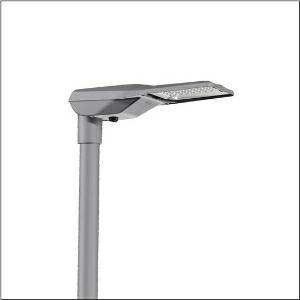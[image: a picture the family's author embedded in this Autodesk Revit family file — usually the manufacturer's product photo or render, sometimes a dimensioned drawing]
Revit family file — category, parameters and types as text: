
# Revit family: streetlight_sl_21_mini___p0_8a_5xe2u33r08gb_ec99
name_source: partatom
category: Lighting Fixtures
units: mm (PartAtom-declared; Revit-internal decimal feet)

## family parameters
Cut with Voids When Loaded = No
Host = Face
Light Source = No
Part Type = Normal
Room Calculation Point = No
Round Connector Dimension = Use Diameter
Shared = No

## types (1)
- --- (1 x LED, 5990 lm, 40.4 W, 3000K)
    Apparent Load = 40 VA
    CIE Flux Codes = 33 69 96 100 100
    Color Rendering = 70
    Color Temperature = 3000K
    Default Elevation = 1800 mm
    Description = Streetlight SL 21 mini, mast luminaire, primary light control with lens, of PMMA, primary optical cover: cover, of toughened safety glass, transparent, light distribution: P0.8a, light emission: direct distribution, primary light characteristic: asymmetric, installation type: post-top, side-entry, LED, High Power LED, rated luminous flux: 5.990lm, luminous efficacy: 148lm/W, light colour: 730, colour temperature: 3000K, control gear: D4i, control: pre-setting: logarithmic dimming characteristic, flexible luminous flux parameterisation, time-dependent luminous flux control, constant luminous flux control, overheat protection, mains connection: 220..240V, AC, 50/60Hz, start of lifetime: 40W, end of service life: 41W, reduction: 19W, luminaire housing, of diecast aluminium, powder-coated, Siteco® metallic grey (DB 702S), corrosivity category C5 mid according to DIN EN ISO 12944, multi-level sealing system, sealing non-destructively replaceable, inclination adjustable: 0°, 5°, 10°, 15°, please order mast flange separately, length: 628mm, width: 235mm, height: 110mm, mast flange for spigot size: 42mm (side-entry): 5XC10008XM4, 60/48mm (side-entry/post-top): 5XC10108XM2, 76/60mm (side-entry/post-top): 5XC10108XM1, mounting height: 4..8m, Smart Interface below, protection rating (complete): IP66, insulation class (complete): insulation class II (safety insulation), certification: CE, ENEC, ENEC+, VDE, impact resistance: IK10, permissible operating ambient temperature for outdoor applications: -40..+50°C, standard-compliant lighting for roads and squares, packaging unit: 1 piece

Light Distribution: P0.8a
    Height = 110 mm
    Lamp = 1 x LED
    Lamp Light Flux = 5990 lm
    Lamp Power = 40.4 W
    Lamp count = 1
    Length = 625 mm
    Luminous efficacy = 148 lm/W
    Manufacturer = Siteco
    ModVariant = No
    Model = 5XE2U33R08GB
    Number of Poles = 1
    OnlyDefault = Yes
    Power Factor = 1
    Product Name = Streetlight SL 21 mini | P0.8a
    Product group = mast luminaire | pylon top
    ProductGroupID = 6100
    Protection Class = Protection class II
    Protection Degree = IP 66
    RLX_Detail_Level = 1
    RLX_Emergency_Light_Flux = 0 lm
    RLX_Emergency_Type = 0
    RLX_Emergency_Type_DB = No
    RlxData = <blob elided: 26005 chars, md5=ea3025d6>
    Socket = socket
    Standby Power = 0 W
    System Light Flux = 5990 lm
    System Power = 40 W
    Type Comments = factory setting: luminous flux: 100 % | dim-lin: 254 | 812 mA
    Type Image = l_1003516.jpg
    URL = http://relux.com
    VarID = @adj_072288
    Voltage = 0 V
    Weight = 0.00 kg
    Width = 234 mm

## geometry (parser evidence)
native form markers: Blend x4, Sweep x11
no freeform markers — native parametric forms only
